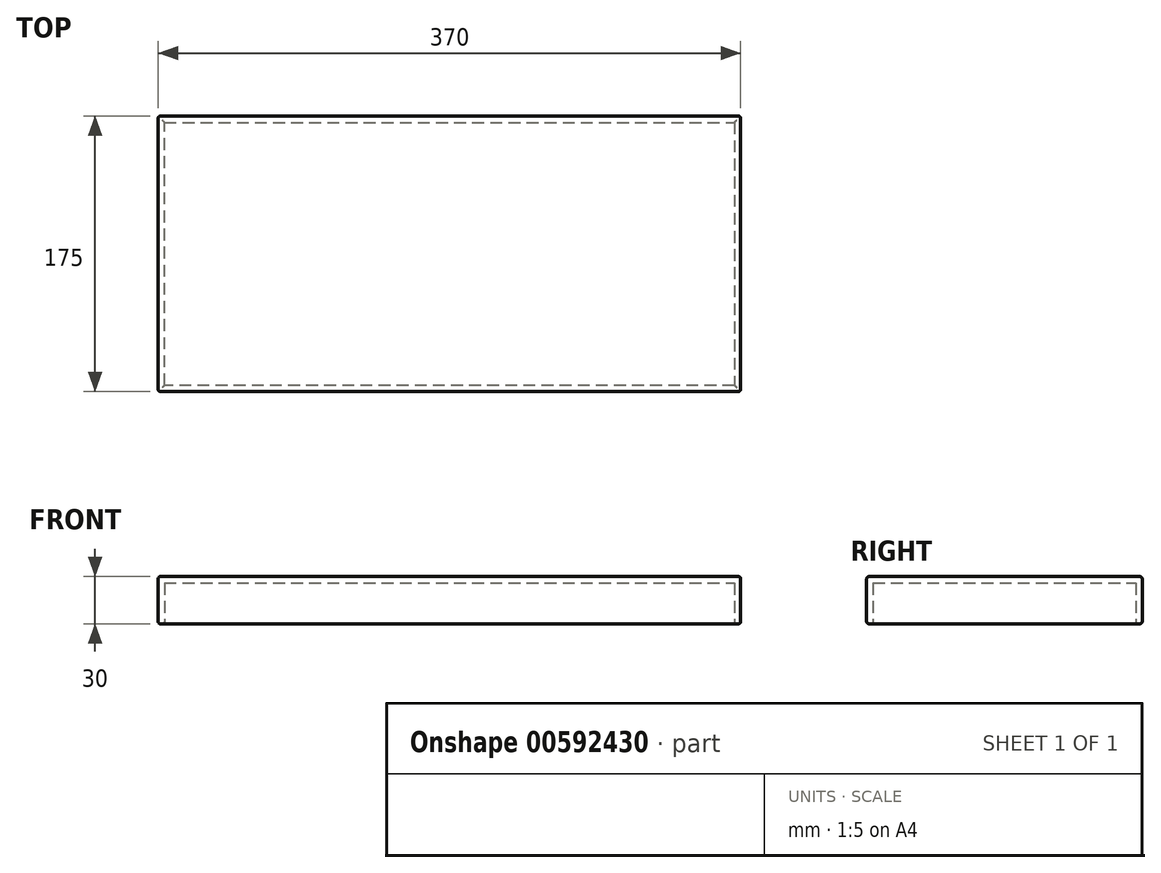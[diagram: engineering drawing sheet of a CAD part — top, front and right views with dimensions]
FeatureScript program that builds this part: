
annotation { "Feature Type Name" : "Feature", "Feature Type Description" : "" }
export const myFeature = defineFeature(function(context is Context, id is Id, definition is map)
    precondition{}
    {
        {
            var Q0;
            Q0=qCreatedBy(makeId("Top.planeOp"),FACE);
            var sketch = newSketch(context, id + "F0", { "sketchPlane" : qUnion([Q0])});
            skLineSegment(sketch, "E0", {"start": v(-56.65, 37.71) * mm, "end": v(313.35, 37.71) * mm});
            skLineSegment(sketch, "E1", {"start": v(313.35, 37.71) * mm, "end": v(313.35, -137.29) * mm});
            skLineSegment(sketch, "E2", {"start": v(313.35, -137.29) * mm, "end": v(-56.65, -137.29) * mm});
            skLineSegment(sketch, "E3", {"start": v(-56.65, -137.29) * mm, "end": v(-56.65, 37.71) * mm});
            skSolve(sketch);
        }
        {
            var Q0;
            Q0 = qSketchRegion(id + "F0", true);
            extrude(context, id + "F1", {"entities" : qUnion([Q0]), "depth" : 30 * mm, "offsetDistance" : 25 * mm});
        }
        {
            var Q0;
            Q0=makeQuery(id+"F1.opExtrude","CAP_FACE",FACE,{"disambiguationData":[OSD([sQuery(id+"F0.wireOp",EDGE,"E0"),sQuery(id+"F0.wireOp",EDGE,"E1"),sQuery(id+"F0.wireOp",EDGE,"E2"),sQuery(id+"F0.wireOp",EDGE,"E3")])],"isStart":true});
            shell(context, id + "F2", {"entities" : qUnion([Q0]), "thickness" : 4 * mm});
        }
        {
            var Q0;
            Q0=makeQuery(id+"F1.opExtrude","CAP_EDGE",EDGE,{"disambiguationData":[OSD([sQuery(id+"F0.wireOp",EDGE,"E2")])],"isStart":true});
            var Q1;
            Q1=makeQuery(id+"F1.opExtrude","CAP_EDGE",EDGE,{"disambiguationData":[OSD([sQuery(id+"F0.wireOp",EDGE,"E3")])],"isStart":true});
            var Q2;
            {var subQ0=sQuery(id+"F0.wireOp",EDGE,"E3");Q2=makeQuery(id+"F2.opShell","OFFSET_EDGE",EDGE,{"disambiguationData":[OSD([subQ0]),TDD([makeQuery(id+"F1.opExtrude","CAP_EDGE",EDGE,{"disambiguationData":[OSD([subQ0])],"isStart":true})])]});}
            var Q3;
            {var subQ0=sQuery(id+"F0.wireOp",EDGE,"E2");Q3=makeQuery(id+"F2.opShell","OFFSET_EDGE",EDGE,{"disambiguationData":[OSD([subQ0]),TDD([makeQuery(id+"F1.opExtrude","CAP_EDGE",EDGE,{"disambiguationData":[OSD([subQ0])],"isStart":true})])]});}
            var Q4;
            Q4=makeQuery(id+"F1.opExtrude","CAP_EDGE",EDGE,{"disambiguationData":[OSD([sQuery(id+"F0.wireOp",EDGE,"E0")])],"isStart":true});
            var Q5;
            {var subQ0=sQuery(id+"F0.wireOp",EDGE,"E0");Q5=makeQuery(id+"F2.opShell","OFFSET_EDGE",EDGE,{"disambiguationData":[OSD([subQ0]),TDD([makeQuery(id+"F1.opExtrude","CAP_EDGE",EDGE,{"disambiguationData":[OSD([subQ0])],"isStart":true})])]});}
            var Q6;
            {var subQ0=sQuery(id+"F0.wireOp",EDGE,"E1");Q6=makeQuery(id+"F2.opShell","OFFSET_EDGE",EDGE,{"disambiguationData":[OSD([subQ0]),TDD([makeQuery(id+"F1.opExtrude","CAP_EDGE",EDGE,{"disambiguationData":[OSD([subQ0])],"isStart":true})])]});}
            var Q7;
            Q7=makeQuery(id+"F1.opExtrude","CAP_EDGE",EDGE,{"disambiguationData":[OSD([sQuery(id+"F0.wireOp",EDGE,"E1")])],"isStart":true});
            fillet(context, id + "F3", {"entities" : qUnion([Q0, Q1, Q2, Q3, Q4, Q5, Q6, Q7]), "radius" : 1.5 * mm, "tangentPropagation" : true, "allowEdgeOverflow" : false});
        }
        {
            var Q0;
            Q0=makeQuery(id+"F1.opExtrude","CAP_EDGE",EDGE,{"disambiguationData":[OSD([sQuery(id+"F0.wireOp",EDGE,"E3")])],"isStart":false});
            var Q1;
            Q1=makeQuery(id+"F1.opExtrude","SWEPT_EDGE",EDGE,{"disambiguationData":[OSD([sQuery(id+"F0.wireOp",EDGE,"E0"),sQuery(id+"F0.wireOp",EDGE,"E3")])]});
            var Q2;
            Q2=makeQuery(id+"F1.opExtrude","SWEPT_EDGE",EDGE,{"disambiguationData":[OSD([sQuery(id+"F0.wireOp",EDGE,"E2"),sQuery(id+"F0.wireOp",EDGE,"E3")])]});
            var Q3;
            Q3=makeQuery(id+"F1.opExtrude","CAP_EDGE",EDGE,{"disambiguationData":[OSD([sQuery(id+"F0.wireOp",EDGE,"E2")])],"isStart":false});
            var Q4;
            Q4=makeQuery(id+"F1.opExtrude","SWEPT_EDGE",EDGE,{"disambiguationData":[OSD([sQuery(id+"F0.wireOp",EDGE,"E1"),sQuery(id+"F0.wireOp",EDGE,"E2")])]});
            var Q5;
            Q5=makeQuery(id+"F1.opExtrude","SWEPT_EDGE",EDGE,{"disambiguationData":[OSD([sQuery(id+"F0.wireOp",EDGE,"E0"),sQuery(id+"F0.wireOp",EDGE,"E1")])]});
            var Q6;
            Q6=makeQuery(id+"F1.opExtrude","CAP_EDGE",EDGE,{"disambiguationData":[OSD([sQuery(id+"F0.wireOp",EDGE,"E0")])],"isStart":false});
            var Q7;
            Q7=makeQuery(id+"F1.opExtrude","CAP_EDGE",EDGE,{"disambiguationData":[OSD([sQuery(id+"F0.wireOp",EDGE,"E1")])],"isStart":false});
            fillet(context, id + "F4", {"entities" : qUnion([Q0, Q1, Q2, Q3, Q4, Q5, Q6, Q7]), "radius" : 1.5 * mm, "tangentPropagation" : true, "allowEdgeOverflow" : false});
        }
    });
